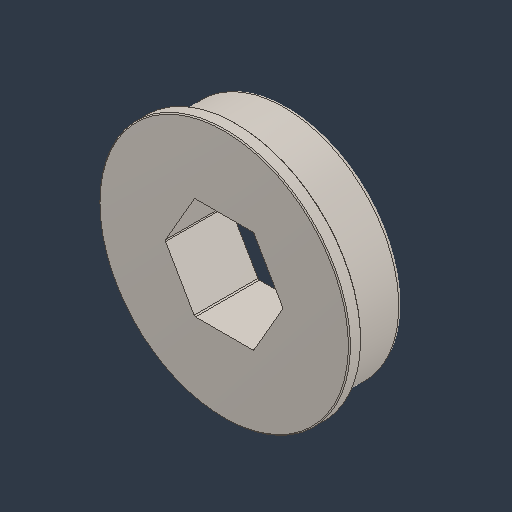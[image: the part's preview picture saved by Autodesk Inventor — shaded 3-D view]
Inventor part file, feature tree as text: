
AUTODESK INVENTOR PART (.ipt)
format: ipt  version: 2024.3 (Build 283343000, 343)  size: 151,552 bytes
history: native  units: in
note: dims shown in document units (in); Inventor stores cm internally (conversion verified against a paired STEP export)
features: fillet x1
ambient origin geometry x8: Origin, YZ Plane, XZ Plane, XY Plane, X Axis, Y Axis, Z Axis, Center Point
bodies: Solid1 (feature_tree)
feature tree (1):
  fillet  "Fillet2"  [1 undecoded]
note: 1 required parameter value undecoded (feature->parameter linkage not recoverable at this tier; creation-order binding heuristic only, values carry confidence <= 0.55)
